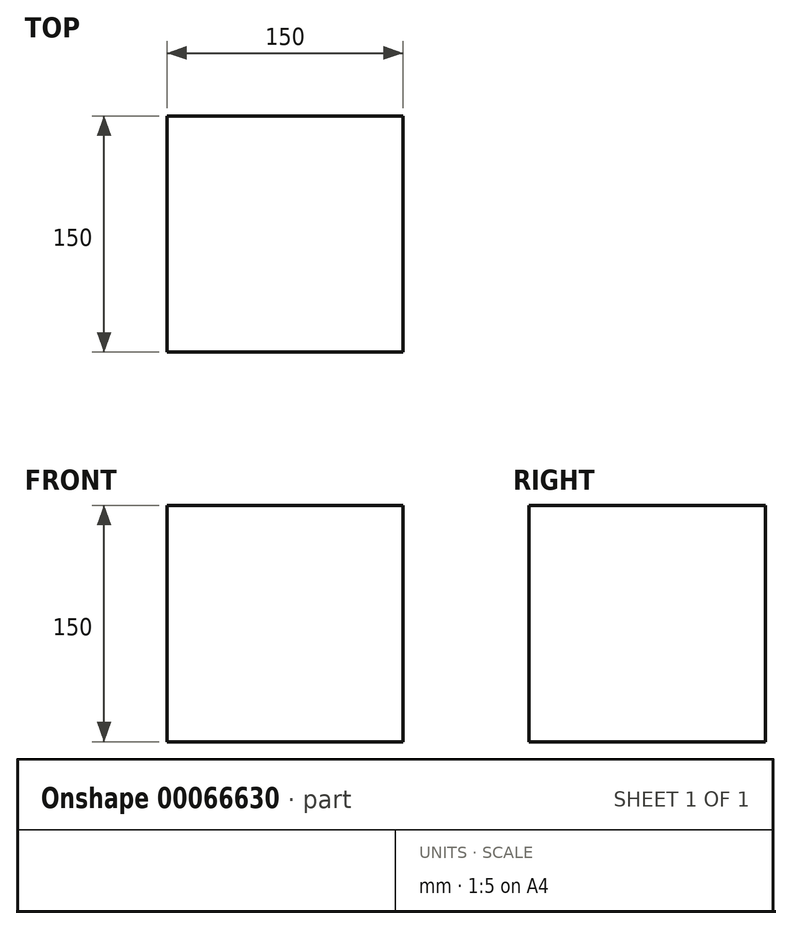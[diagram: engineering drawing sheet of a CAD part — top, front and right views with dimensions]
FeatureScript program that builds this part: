
annotation { "Feature Type Name" : "Feature", "Feature Type Description" : "" }
export const myFeature = defineFeature(function(context is Context, id is Id, definition is map)
    precondition{}
    {
        {
            var Q0;
            Q0=qCreatedBy(makeId("Front.planeOp"),FACE);
            var sketch = newSketch(context, id + "F0", { "sketchPlane" : qUnion([Q0])});
            skLineSegment(sketch, "E0.bottom", {"start": v(-75, 75) * mm, "end": v(75, 75) * mm});
            skLineSegment(sketch, "E0.top", {"start": v(-75, -75) * mm, "end": v(75, -75) * mm});
            skLineSegment(sketch, "E0.left", {"start": v(-75, 75) * mm, "end": v(-75, -75) * mm});
            skLineSegment(sketch, "E0.right", {"start": v(75, 75) * mm, "end": v(75, -75) * mm});
            skSolve(sketch);
        }
        {
            var Q0;
            Q0 = qSketchRegion(id + "F0", true);
            extrude(context, id + "F1", {"entities" : qUnion([Q0]), "depth" : 150 * mm});
        }
    });
